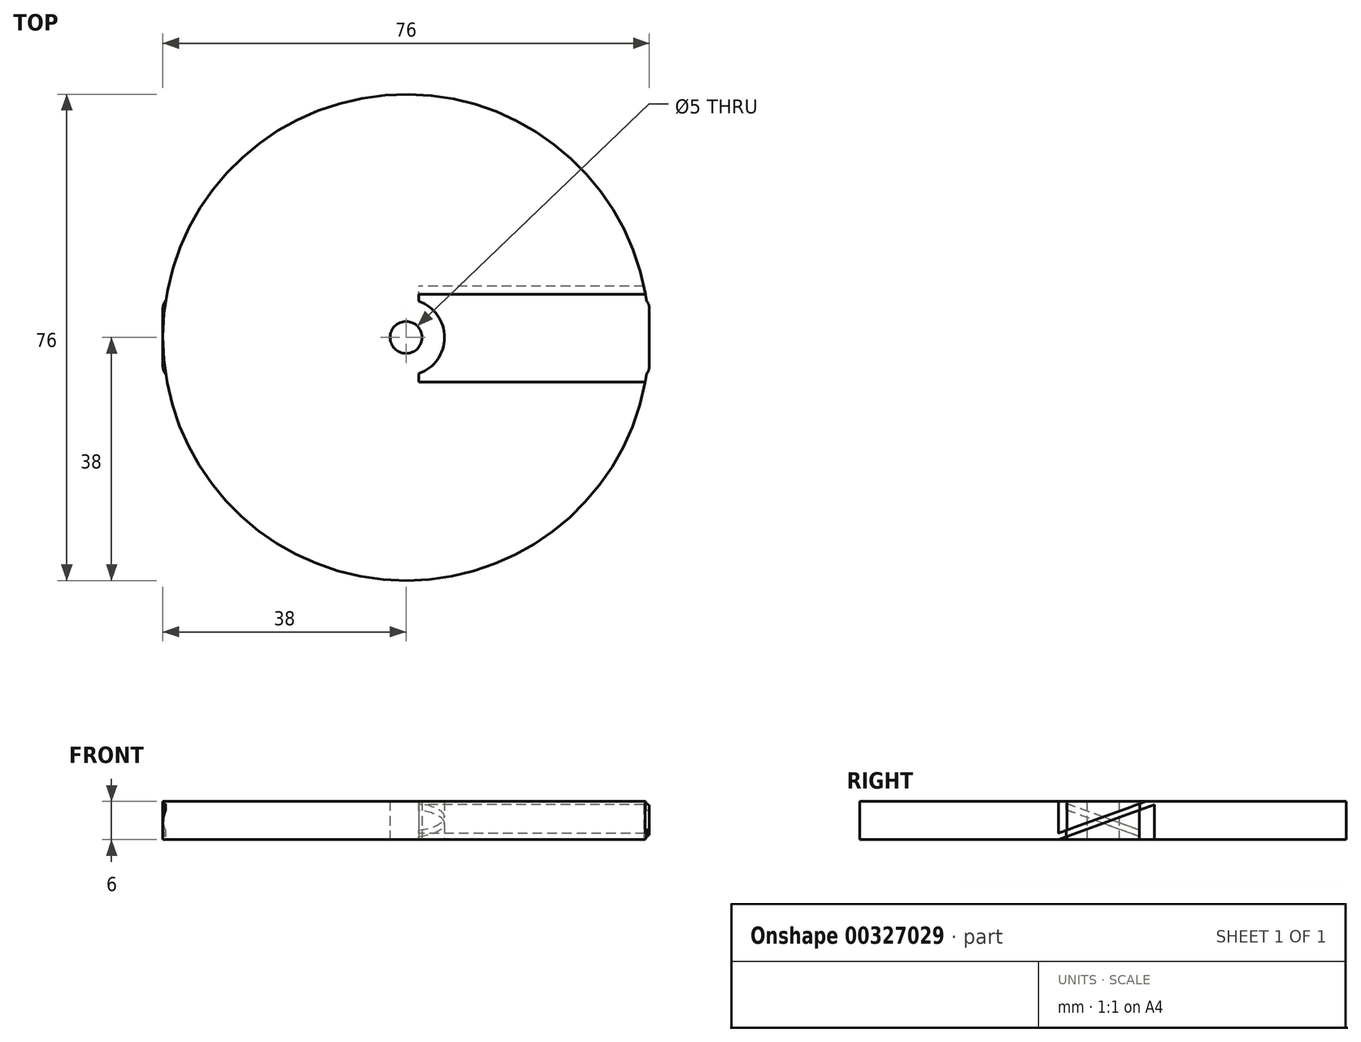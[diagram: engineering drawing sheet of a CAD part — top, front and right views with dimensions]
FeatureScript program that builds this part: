
annotation { "Feature Type Name" : "Feature", "Feature Type Description" : "" }
export const myFeature = defineFeature(function(context is Context, id is Id, definition is map)
    precondition{}
    {
        {
            var Q0;
            Q0=qCreatedBy(makeId("Top.planeOp"),FACE);
            var sketch = newSketch(context, id + "F0", { "sketchPlane" : qUnion([Q0])});
            skCircle(sketch, "E0", {"center": v(0, 0) * mm, "radius": 2.5 * mm});
            skCircle(sketch, "E1", {"center": v(0, 0) * mm, "radius": 6 * mm});
            skCircle(sketch, "E2", {"center": v(0, 0) * mm, "radius": 38 * mm});
            skSolve(sketch);
        }
        {
            var Q0;
            Q0=makeQuery(id+"F0.imprint","IMPRINT",FACE,{"disambiguationData":[TD([[makeQuery(id+"F0.imprint","IMPRINT",EDGE,{"derivedFrom":sQuery(id+"F0.wireOp",EDGE,"E0")}),-1.0]])]});
            extrude(context, id + "F1", {"entities" : qUnion([Q0]), "depth" : 6 * mm});
        }
        {
            var Q0;
            Q0=makeQuery(id+"F0.imprint","IMPRINT",FACE,{"disambiguationData":[TD([[makeQuery(id+"F0.imprint","IMPRINT",EDGE,{"derivedFrom":sQuery(id+"F0.wireOp",EDGE,"E1")}),-1.0]])]});
            extrude(context, id + "F2", {"entities" : qUnion([Q0]), "depth" : 6 * mm});
        }
        {
            var Q0;
            Q0=qCreatedBy(makeId("Top.planeOp"),FACE);
            var sketch = newSketch(context, id + "F3", { "sketchPlane" : qUnion([Q0])});
            skLineSegment(sketch, "E3.bottom", {"start": v(38, 6.5) * mm, "end": v(0, 6.5) * mm});
            skLineSegment(sketch, "E3.top", {"start": v(38, -6.5) * mm, "end": v(0, -6.5) * mm});
            skLineSegment(sketch, "E3.left", {"start": v(38, 6.5) * mm, "end": v(38, -6.5) * mm});
            skLineSegment(sketch, "E3.right", {"start": v(0, 6.5) * mm, "end": v(0, -6.5) * mm});
            skPoint(sketch, "E3.middle", {"position": v(19, 0) * mm});
            skSolve(sketch);
        }
        {
            var Q0;
            Q0 = qSketchRegion(id + "F3", true);
            extrude(context, id + "F4", {"entities" : qUnion([Q0]), "depth" : 6 * mm});
        }
        {
            var Q0;
            Q0=makeQuery(id+"F4.opExtrude","SWEPT_EDGE",EDGE,{"disambiguationData":[OSD([sQuery(id+"F3.wireOp",EDGE,"E3.bottom"),sQuery(id+"F3.wireOp",EDGE,"E3.right")])]});
            var Q1;
            Q1=makeQuery(id+"F4.opExtrude","SWEPT_EDGE",EDGE,{"disambiguationData":[OSD([sQuery(id+"F3.wireOp",EDGE,"E3.top"),sQuery(id+"F3.wireOp",EDGE,"E3.right")])]});
            fillet(context, id + "F5", {"entities" : qUnion([Q0, Q1]), "radius" : 5 * mm, "tangentPropagation" : true, "allowEdgeOverflow" : false});
        }
        {
            var Q0;
            Q0=makeQuery(id+"F4.opExtrude","SWEPT_EDGE",EDGE,{"disambiguationData":[OSD([sQuery(id+"F3.wireOp",EDGE,"E3.bottom"),sQuery(id+"F3.wireOp",EDGE,"E3.left")])]});
            var Q1;
            Q1=makeQuery(id+"F4.opExtrude","SWEPT_EDGE",EDGE,{"disambiguationData":[OSD([sQuery(id+"F3.wireOp",EDGE,"E3.top"),sQuery(id+"F3.wireOp",EDGE,"E3.left")])]});
            fillet(context, id + "F6", {"entities" : qUnion([Q0, Q1]), "radius" : 2 * mm, "tangentPropagation" : true, "allowEdgeOverflow" : false});
        }
        {
            var Q0;
            Q0=qCreatedBy(makeId("Right.planeOp"),FACE);
            var sketch = newSketch(context, id + "F7", { "sketchPlane" : qUnion([Q0])});
            skLineSegment(sketch, "E4", {"start": v(-7, 1) * mm, "end": v(8, 6.46) * mm});
            skLineSegment(sketch, "E5", {"start": v(8, 6.46) * mm, "end": v(8, 7) * mm});
            skLineSegment(sketch, "E6", {"start": v(8, 7) * mm, "end": v(-7, 7) * mm});
            skLineSegment(sketch, "E7", {"start": v(-7, 7) * mm, "end": v(-7, 1) * mm});
            skLineSegment(sketch, "E8", {"start": v(-7, 0) * mm, "end": v(8, 5.46) * mm});
            skLineSegment(sketch, "E9", {"start": v(8, 5.46) * mm, "end": v(8, -5) * mm});
            skLineSegment(sketch, "E10", {"start": v(8, -5) * mm, "end": v(-7, -5) * mm});
            skLineSegment(sketch, "E11", {"start": v(-7, -5) * mm, "end": v(-7, 0) * mm});
            skSolve(sketch);
        }
        {
            var Q0;
            Q0 = qSketchRegion(id + "F7", true);
            var Q1;
            Q1=makeQuery(id+"F4.opExtrude","SWEPT_FACE",FACE,{"disambiguationData":[OSD([sQuery(id+"F3.wireOp",EDGE,"E3.left")])]});
            extrude(context, id + "F8", {"entities" : qUnion([Q0]), "operationType" : NewBodyOperationType.REMOVE, "endBound" : BoundingType.UP_TO_SURFACE, "endBoundEntityFace" : qUnion([Q1]), "depth" : 40 * mm, "hasSecondDirection" : true, "secondDirectionOppositeDirection" : false, "secondDirectionDepth" : 2 * mm});
        }
        {
            var Q0;
            Q0=qCreatedBy(makeId("Front.planeOp"),FACE);
            var sketch = newSketch(context, id + "F9", { "sketchPlane" : qUnion([Q0])});
            skLineSegment(sketch, "E12", {"start": v(0, 15) * mm, "end": v(0, -15) * mm, "construction": true});
            skSolve(sketch);
        }
        {
            var Q0;
            Q0=makeQuery(id+"F1.opExtrude","SWEPT_BODY",BODY,{"disambiguationData":[OSD([sQuery(id+"F0.wireOp",EDGE,"E0"),sQuery(id+"F0.wireOp",EDGE,"E1")])]});
            var Q1;
            Q1=makeQuery(id+"F4.opExtrude","SWEPT_BODY",BODY,{"disambiguationData":[OSD([sQuery(id+"F3.wireOp",EDGE,"E3.bottom"),sQuery(id+"F3.wireOp",EDGE,"E3.top"),sQuery(id+"F3.wireOp",EDGE,"E3.left"),sQuery(id+"F3.wireOp",EDGE,"E3.right")])]});
            var Q2;
            Q2=sQuery(id+"F9.wireOp",EDGE,"E12");
            circularPattern(context, id + "F10", {"operationType" : NewBodyOperationType.ADD, "entities" : qUnion([Q0, Q1]), "axis" : qUnion([Q2]), "angle" : 360 * degree, "instanceCount" : 2, "equalSpace" : true});
        }
        {
            var Q0;
            Q0=makeQuery(id+"F0.imprint","IMPRINT",FACE,{"disambiguationData":[TD([[makeQuery(id+"F0.imprint","IMPRINT",EDGE,{"derivedFrom":sQuery(id+"F0.wireOp",EDGE,"E0")}),1.0]])]});
            var Q1;
            {var subQ0=makeQuery(id+"F4.opExtrude","CAP_FACE",FACE,{"disambiguationData":[OSD([sQuery(id+"F3.wireOp",EDGE,"E3.bottom"),sQuery(id+"F3.wireOp",EDGE,"E3.top"),sQuery(id+"F3.wireOp",EDGE,"E3.left"),sQuery(id+"F3.wireOp",EDGE,"E3.right")])],"isStart":false});var subQ1=makeQuery(id+"F1.opExtrude","CAP_FACE",FACE,{"disambiguationData":[OSD([sQuery(id+"F0.wireOp",EDGE,"E0"),sQuery(id+"F0.wireOp",EDGE,"E1")])],"isStart":false});Q1=makeQuery(id+"F10.boolean.opBoolean","MERGE",FACE,{"derivedFrom":[subQ1,subQ0,makeQuery(id+"F10.opPattern","COPY",FACE,{"derivedFrom":subQ1,"instanceName":"1"}),makeQuery(id+"F10.opPattern","COPY",FACE,{"derivedFrom":subQ0,"instanceName":"1"})]});}
            extrude(context, id + "F11", {"entities" : qUnion([Q0]), "operationType" : NewBodyOperationType.REMOVE, "endBound" : BoundingType.UP_TO_SURFACE, "endBoundEntityFace" : qUnion([Q1]), "depth" : 25 * mm});
        }
    });
